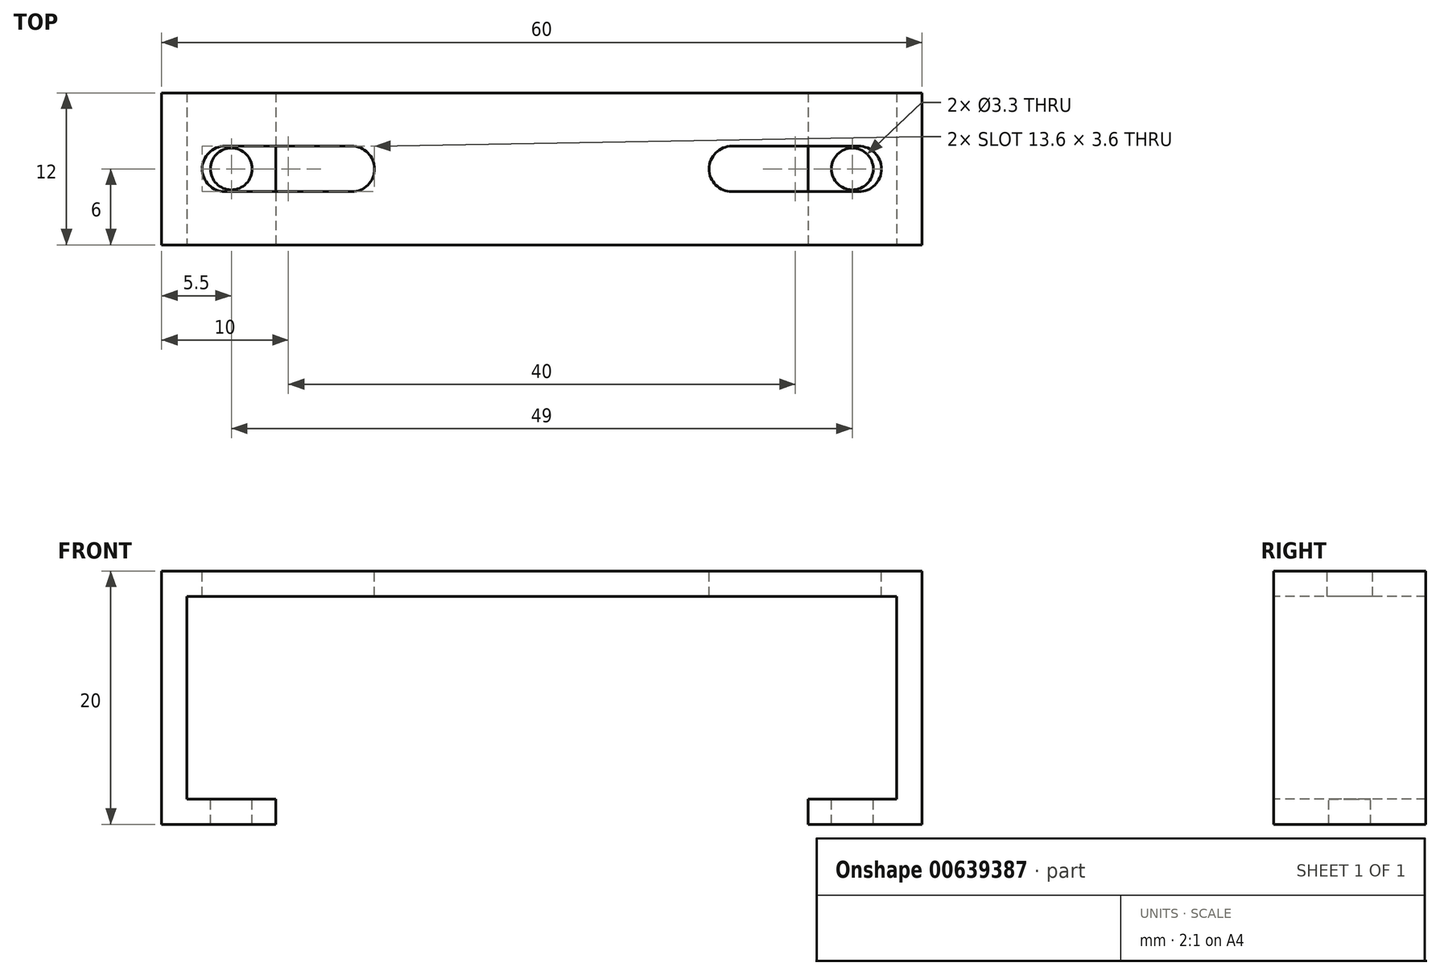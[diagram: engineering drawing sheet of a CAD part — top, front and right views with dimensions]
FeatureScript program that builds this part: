
annotation { "Feature Type Name" : "Feature", "Feature Type Description" : "" }
export const myFeature = defineFeature(function(context is Context, id is Id, definition is map)
    precondition{}
    {
        {
            var Q0;
            Q0=qCreatedBy(makeId("Top.planeOp"),FACE);
            var sketch = newSketch(context, id + "F0", { "sketchPlane" : qUnion([Q0])});
            skLineSegment(sketch, "E0.bottom", {"start": v(-30, 6) * mm, "end": v(30, 6) * mm});
            skLineSegment(sketch, "E0.top", {"start": v(-30, -6) * mm, "end": v(30, -6) * mm});
            skLineSegment(sketch, "E0.left", {"start": v(-30, 6) * mm, "end": v(-30, -6) * mm});
            skLineSegment(sketch, "E0.right", {"start": v(30, 6) * mm, "end": v(30, -6) * mm});
            skSolve(sketch);
        }
        {
            var Q0;
            Q0 = qSketchRegion(id + "F0", true);
            extrude(context, id + "F1", {"entities" : qUnion([Q0]), "depth" : 20 * mm, "offsetDistance" : 25 * mm});
        }
        {
            var Q0;
            Q0=makeQuery(id+"F1.opExtrude","SWEPT_FACE",FACE,{"disambiguationData":[OSD([sQuery(id+"F0.wireOp",EDGE,"E0.top")])]});
            var sketch = newSketch(context, id + "F2", { "sketchPlane" : qUnion([Q0])});
            skLineSegment(sketch, "E1.bottom", {"start": v(-28, 18) * mm, "end": v(28, 18) * mm});
            skLineSegment(sketch, "E1.top", {"start": v(-28, 2) * mm, "end": v(28, 2) * mm});
            skLineSegment(sketch, "E1.left", {"start": v(-28, 18) * mm, "end": v(-28, 2) * mm});
            skLineSegment(sketch, "E1.right", {"start": v(28, 18) * mm, "end": v(28, 2) * mm});
            skLineSegment(sketch, "E2.bottom", {"start": v(-21, 2) * mm, "end": v(21, 2) * mm});
            skLineSegment(sketch, "E2.top", {"start": v(-21, 0) * mm, "end": v(21, 0) * mm});
            skLineSegment(sketch, "E2.left", {"start": v(-21, 2) * mm, "end": v(-21, 0) * mm});
            skLineSegment(sketch, "E2.right", {"start": v(21, 2) * mm, "end": v(21, 0) * mm});
            skSolve(sketch);
        }
        {
            var Q0;
            Q0 = qSketchRegion(id + "F2", true);
            extrude(context, id + "F3", {"entities" : qUnion([Q0]), "operationType" : NewBodyOperationType.REMOVE, "endBound" : BoundingType.THROUGH_ALL, "oppositeDirection" : true, "depth" : 25 * mm, "offsetDistance" : 25 * mm});
        }
        {
            var Q0;
            Q0 = qSketchRegion(id + "F2", true);
            extrude(context, id + "F4", {"entities" : qUnion([Q0]), "operationType" : NewBodyOperationType.REMOVE, "endBound" : BoundingType.THROUGH_ALL, "oppositeDirection" : true, "depth" : 25 * mm, "offsetDistance" : 25 * mm});
        }
        {
            var Q0;
            {var subQ0=sQuery(id+"F2.wireOp",EDGE,"E1.top");Q0=makeQuery(id+"F3.boolean.opBoolean","COPY",FACE,{"derivedFrom":makeQuery(id+"F3.opExtrude","SWEPT_FACE",FACE,{"disambiguationData":[OSD([subQ0]),TDD([makeQuery(id+"F2.imprint","IMPRINT",EDGE,{"disambiguationData":[TD([[makeQuery(id+"F2.imprint","INTERSECT",VERTEX,{"derivedFrom":[subQ0,sQuery(id+"F2.wireOp",EDGE,"E1.left")]}),-1.0]])],"derivedFrom":subQ0})])]})});}
            var sketch = newSketch(context, id + "F5", { "sketchPlane" : qUnion([Q0])});
            skPoint(sketch, "E3", {"position": v(-24.5, 0) * mm});
            skSolve(sketch);
        }
        {
            var Q0;
            Q0=sQuery(id+"F5.wireOp",VERTEX,"E3");
            var Q1;
            Q1=makeQuery(id+"F1.opExtrude","SWEPT_BODY",BODY,{"disambiguationData":[OSD([sQuery(id+"F0.wireOp",EDGE,"E0.bottom"),sQuery(id+"F0.wireOp",EDGE,"E0.top"),sQuery(id+"F0.wireOp",EDGE,"E0.left"),sQuery(id+"F0.wireOp",EDGE,"E0.right")])]});
            hole(context, id + "F6", {"style" : HoleStyle.SIMPLE, "endStyle" : HoleEndStyle.THROUGH, "standardTappedOrClearance" : lookupTablePath({ "standard" : "ISO", "fit" : "Normal", "size" : "M3", "type" : "Clearance" }), "standardBlindInLast" : lookupTablePath({ "fit" : "Standard", "standard" : "ISO", "size" : "M3", "type" : "Clearance" }), "holeDiameter" : 3.3 * mm, "majorDiameter" : 5 * mm, "isTappedThrough" : true, "tappedDepth" : 12 * mm, "tapClearance" : 3, "locations" : qUnion([Q0]), "scope" : qUnion([Q1])});
        }
        {
            var Q0;
            {var subQ0=sQuery(id+"F2.wireOp",EDGE,"E1.top");Q0=makeQuery(id+"F3.boolean.opBoolean","COPY",FACE,{"derivedFrom":makeQuery(id+"F3.opExtrude","SWEPT_FACE",FACE,{"disambiguationData":[OSD([subQ0]),TDD([makeQuery(id+"F2.imprint","IMPRINT",EDGE,{"disambiguationData":[TD([[makeQuery(id+"F2.imprint","INTERSECT",VERTEX,{"derivedFrom":[subQ0,sQuery(id+"F2.wireOp",EDGE,"E1.right")]}),1.0]])],"derivedFrom":subQ0})])]})});}
            var sketch = newSketch(context, id + "F7", { "sketchPlane" : qUnion([Q0])});
            skPoint(sketch, "E4", {"position": v(24.5, 0) * mm});
            skPoint(sketch, "E4.positionSnap0", {"position": v(28, 0) * mm});
            skPoint(sketch, "E4.positionSnap1", {"position": v(24.5, 6) * mm});
            skSolve(sketch);
        }
        {
            var Q0;
            Q0=sQuery(id+"F7.wireOp",VERTEX,"E4");
            var Q1;
            Q1=makeQuery(id+"F1.opExtrude","SWEPT_BODY",BODY,{"disambiguationData":[OSD([sQuery(id+"F0.wireOp",EDGE,"E0.bottom"),sQuery(id+"F0.wireOp",EDGE,"E0.top"),sQuery(id+"F0.wireOp",EDGE,"E0.left"),sQuery(id+"F0.wireOp",EDGE,"E0.right")])]});
            hole(context, id + "F8", {"style" : HoleStyle.SIMPLE, "endStyle" : HoleEndStyle.THROUGH, "standardTappedOrClearance" : lookupTablePath({ "standard" : "ISO", "fit" : "Normal", "size" : "M3", "type" : "Clearance" }), "standardBlindInLast" : lookupTablePath({ "fit" : "Standard", "standard" : "ISO", "size" : "M3", "type" : "Clearance" }), "holeDiameter" : 3.3 * mm, "majorDiameter" : 5 * mm, "isTappedThrough" : true, "tappedDepth" : 12 * mm, "tapClearance" : 3, "locations" : qUnion([Q0]), "scope" : qUnion([Q1])});
        }
        {
            var Q0;
            Q0=makeQuery(id+"F1.opExtrude","CAP_FACE",FACE,{"disambiguationData":[OSD([sQuery(id+"F0.wireOp",EDGE,"E0.bottom"),sQuery(id+"F0.wireOp",EDGE,"E0.top"),sQuery(id+"F0.wireOp",EDGE,"E0.left"),sQuery(id+"F0.wireOp",EDGE,"E0.right")])],"isStart":false});
            var sketch = newSketch(context, id + "F9", { "sketchPlane" : qUnion([Q0])});
            skPoint(sketch, "E5", {"position": v(15, 0) * mm});
            skPoint(sketch, "E6", {"position": v(-15, 0) * mm});
            skPoint(sketch, "E7", {"position": v(-25, 0) * mm});
            skPoint(sketch, "E8", {"position": v(25, 0) * mm});
            skLineSegment(sketch, "E9.bottom", {"start": v(-25, 1.8) * mm, "end": v(-15, 1.8) * mm});
            skLineSegment(sketch, "E9.top", {"start": v(-25, -1.8) * mm, "end": v(-15, -1.8) * mm});
            skLineSegment(sketch, "E9.left", {"start": v(-25, 1.8) * mm, "end": v(-25, -1.8) * mm});
            skLineSegment(sketch, "E9.right", {"start": v(-15, 1.8) * mm, "end": v(-15, -1.8) * mm});
            skLineSegment(sketch, "E10.bottom", {"start": v(15, 1.8) * mm, "end": v(25, 1.8) * mm});
            skLineSegment(sketch, "E10.top", {"start": v(15, -1.8) * mm, "end": v(25, -1.8) * mm});
            skLineSegment(sketch, "E10.left", {"start": v(15, 1.8) * mm, "end": v(15, -1.8) * mm});
            skLineSegment(sketch, "E10.right", {"start": v(25, 1.8) * mm, "end": v(25, -1.8) * mm});
            skSolve(sketch);
        }
        {
            var Q0;
            Q0=sQuery(id+"F9.wireOp",VERTEX,"E6");
            var Q1;
            Q1=sQuery(id+"F9.wireOp",VERTEX,"E5");
            var Q2;
            Q2=sQuery(id+"F9.wireOp",VERTEX,"E7");
            var Q3;
            Q3=sQuery(id+"F9.wireOp",VERTEX,"E8");
            var Q4;
            Q4=makeQuery(id+"F1.opExtrude","SWEPT_BODY",BODY,{"disambiguationData":[OSD([sQuery(id+"F0.wireOp",EDGE,"E0.bottom"),sQuery(id+"F0.wireOp",EDGE,"E0.top"),sQuery(id+"F0.wireOp",EDGE,"E0.left"),sQuery(id+"F0.wireOp",EDGE,"E0.right")])]});
            hole(context, id + "F10", {"style" : HoleStyle.SIMPLE, "endStyle" : HoleEndStyle.BLIND, "holeDiameter" : 3.6 * mm, "majorDiameter" : 5 * mm, "holeDepth" : 12 * mm, "isTappedThrough" : true, "tappedDepth" : 12 * mm, "tapClearance" : 3, "locations" : qUnion([Q0, Q1, Q2, Q3]), "scope" : qUnion([Q4])});
        }
        {
            var Q0;
            Q0 = qSketchRegion(id + "F9", true);
            extrude(context, id + "F11", {"entities" : qUnion([Q0]), "operationType" : NewBodyOperationType.REMOVE, "endBound" : BoundingType.SYMMETRIC, "oppositeDirection" : true, "depth" : 25 * mm, "offsetDistance" : 25 * mm});
        }
    });
